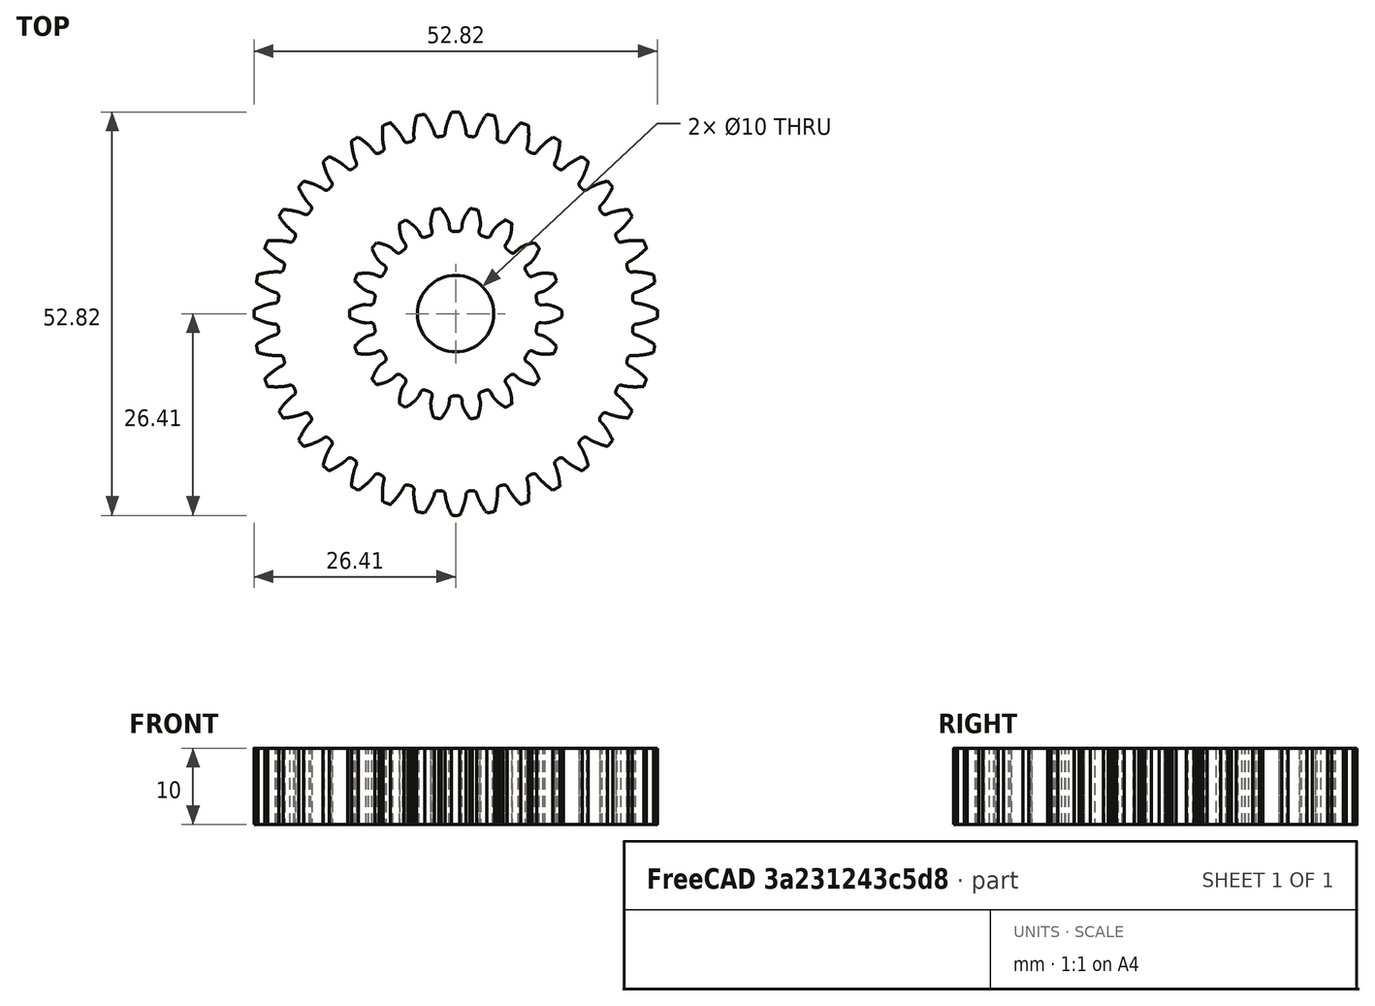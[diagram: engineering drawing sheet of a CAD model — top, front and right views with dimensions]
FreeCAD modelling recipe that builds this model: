
FCSTD DOCUMENT  (FreeCAD 0.19R23756 (Git))
Label: tutorial gear
License: All rights reserved
LicenseURL: http://en.wikipedia.org/wiki/All_rights_reserved
objects: Part::Part2DObjectPython×2, PartDesign::Pad×2, PartDesign::Body×2, Part::Cylinder×2, Part::Cut×2, App::Part×2
note: 12 computed .brp shape members not serialized (recipe doc carries the construction recipe); baked Part::Feature solids carry a one-line shape summary decoded from their .brp

FEATURE [Part::Part2DObjectPython] InvoluteGear  # Draft 2D object (typed FeaturePython)
  ExternalGear = true
  HighPrecision = true
  Modules = 1.39
  NumberOfTeeth = 36
  PressureAngle = 20
FEATURE [PartDesign::Pad] Pad
  Direction = (1,1,1)
  Length = 10
  Length2 = 100
  Profile = -> InvoluteGear
  Type = 0
FEATURE [PartDesign::Body] Body
  Group = -> [InvoluteGear,Pad]
  Origin = -> Origin001
  Tip = -> Pad
FEATURE [Part::Cylinder] Cylinder
  Angle = 360
  AttacherType = Attacher::AttachEngine3D
  Height = 10
  Radius = 5
FEATURE [Part::Cut] Cut
  Base = -> Body
  Tool = -> Cylinder
FEATURE [App::Part] Part  label="gear 1"
  Group = -> [Body,Cylinder,Cut]
  Origin = -> Origin
FEATURE [PartDesign::Body] Body001
  Origin = -> Origin003
FEATURE [Part::Part2DObjectPython] InvoluteGear001  # Draft 2D object (typed FeaturePython)
  ExternalGear = true
  HighPrecision = true
  Modules = 1.39
  NumberOfTeeth = 18
  PressureAngle = 20
FEATURE [PartDesign::Pad] Pad001
  Direction = (1,1,1)
  Length = 10
  Length2 = 100
  Profile = -> InvoluteGear001
  Type = 0
FEATURE [Part::Cylinder] Cylinder001
  Angle = 360
  AttacherType = Attacher::AttachEngine3D
  Height = 10
  Radius = 5
FEATURE [Part::Cut] Cut001
  Base = -> Pad001
  Tool = -> Cylinder001
FEATURE [App::Part] Part001  label="gear 2"
  Group = -> [Body001,Cylinder001,Pad001,InvoluteGear001,Cut001]
  Origin = -> Origin002
  Placement = pos=(37.53,0,0) rot=(0,0,1;0.174533rad)
